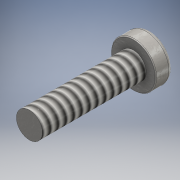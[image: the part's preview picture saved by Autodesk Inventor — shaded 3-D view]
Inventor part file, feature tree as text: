
AUTODESK INVENTOR PART (.ipt)
format: ipt  version: 2016 (Build 200138000, 138)  size: 194,048 bytes
history: native  units: mm
features: extrude x3, sketch x3, fillet x2, thread x1
ambient origin geometry x8: Origin, YZ Plane, XZ Plane, XY Plane, X Axis, Y Axis, Z Axis, Center Point
bodies: Solid1 (feature_tree)
feature tree (9):
  extrude  "Extrusion1"  Depth=12.0mm TaperAngle=0.0deg
  extrude  "Extrusion2"  Depth=2.0mm TaperAngle=0.0deg
  extrude  "Extrusion3"  Depth=1.0mm
  fillet  "Fillet1"  Radius=1.0mm
  fillet  "Fillet2"  Radius=1.0mm
  thread  "Thread1"  [1 undecoded]
  sketch  "Sketch1"  dims[d0=3.0mm d1=12.0mm d2=0.0mm]
  sketch  "Sketch2"  dims[d3=5.2mm d4=2.0mm d5=0.0mm]
  sketch  "Sketch3"  dims[d6=1.0mm d7=1.0mm d8=1.0mm d9=1.0mm d11=1.0mm d12=1.0mm d13=1.0mm d14=1.0mm d15=1.0mm d16=1.0mm d17=135.0deg d18=135.0deg d19=135.0deg d20=0.5mm d21=0.5mm d22=1.8mm d23=1.8mm d24=0.5mm d25=0.8mm d26=0.0mm d27=0.5mm d31=0.1mm d32=10.0mm d33=0.0mm]
note: 1 required parameter value undecoded (feature->parameter linkage not recoverable at this tier; creation-order binding heuristic only, values carry confidence <= 0.55)
